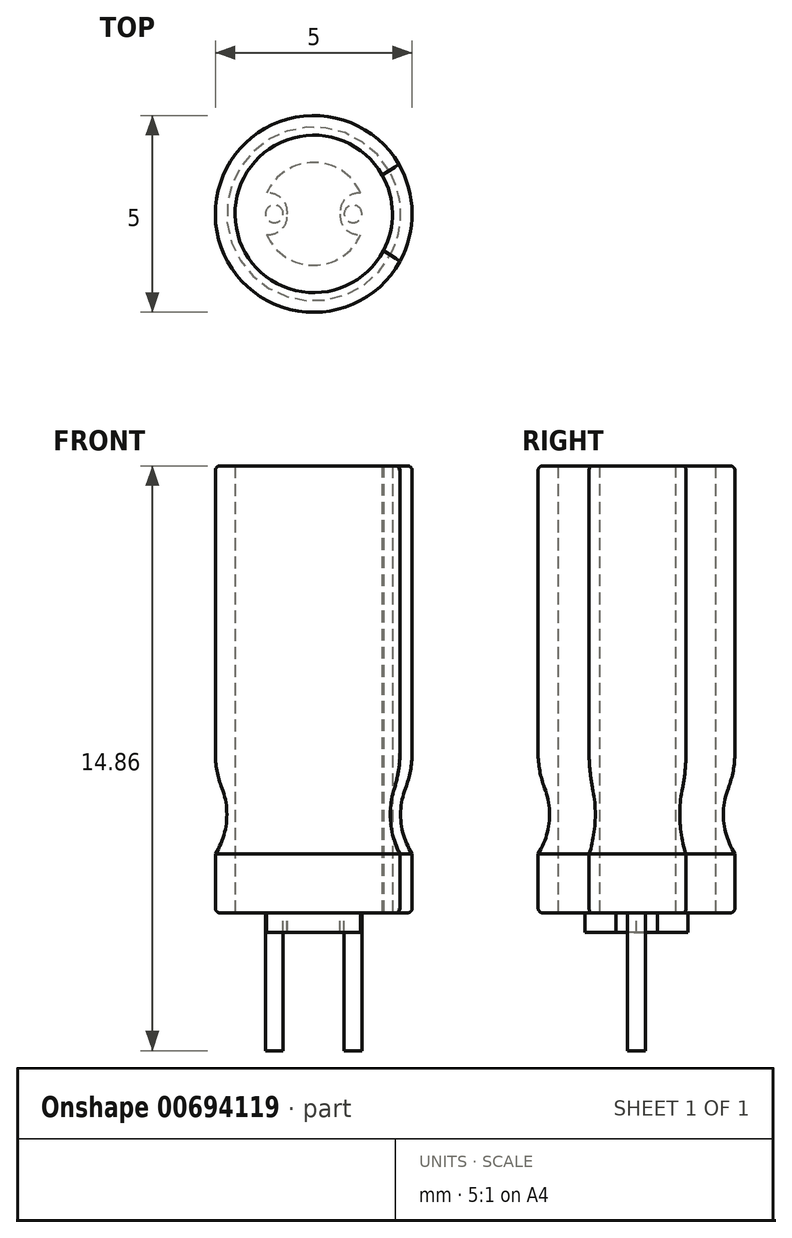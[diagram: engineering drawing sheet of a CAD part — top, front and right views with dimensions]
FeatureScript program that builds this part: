
annotation { "Feature Type Name" : "Feature", "Feature Type Description" : "" }
export const myFeature = defineFeature(function(context is Context, id is Id, definition is map)
    precondition{}
    {
        {
            var Q0;
            Q0=qCreatedBy(makeId("Top.planeOp"),FACE);
            var sketch = newSketch(context, id + "F0", { "sketchPlane" : qUnion([Q0])});
            skCircle(sketch, "E0", {"center": v(0, 0) * mm, "radius": 2.5 * mm});
            skCircle(sketch, "E1", {"center": v(0, 0) * mm, "radius": 2 * mm});
            skLineSegment(sketch, "E2", {"start": v(1.74, 0.99) * mm, "end": v(2.16, 1.26) * mm});
            skLineSegment(sketch, "E3", {"start": v(1.77, -0.93) * mm, "end": v(2.2, -1.2) * mm});
            skSolve(sketch);
        }
        {
            var Q0;
            Q0=qCreatedBy(makeId("Top.planeOp"),FACE);
            var sketch = newSketch(context, id + "F1", { "sketchPlane" : qUnion([Q0])});
            skCircle(sketch, "E4", {"center": v(-1, 0) * mm, "radius": 0.23 * mm});
            skCircle(sketch, "E5", {"center": v(1, 0) * mm, "radius": 0.23 * mm});
            skSolve(sketch);
        }
        {
            var Q0;
            {var subQ0=sQuery(id+"F0.wireOp",EDGE,"E1");var subQ1=makeQuery(id+"F0.imprint","INTERSECT",VERTEX,{"derivedFrom":[subQ0,sQuery(id+"F0.wireOp",EDGE,"E2")]});Q0=makeQuery(id+"F0.imprint","IMPRINT",FACE,{"disambiguationData":[TD([[makeQuery(id+"F0.imprint","IMPRINT",EDGE,{"disambiguationData":[TD([[subQ1,-1.0]])],"derivedFrom":subQ0}),1.0]])]});}
            extrude(context, id + "F2", {"entities" : qUnion([Q0]), "depth" : 11.35 * mm, "offsetDistance" : 25 * mm});
        }
        {
            var Q0;
            {var subQ0=sQuery(id+"F0.wireOp",EDGE,"E2");Q0=makeQuery(id+"F0.imprint","IMPRINT",FACE,{"disambiguationData":[TD([[makeQuery(id+"F0.imprint","IMPRINT",EDGE,{"derivedFrom":subQ0}),1.0]])]});}
            extrude(context, id + "F3", {"entities" : qUnion([Q0]), "depth" : 11.36 * mm, "offsetDistance" : 25 * mm});
        }
        {
            var Q0;
            {var subQ0=sQuery(id+"F0.wireOp",EDGE,"E2");Q0=makeQuery(id+"F0.imprint","IMPRINT",FACE,{"disambiguationData":[TD([[makeQuery(id+"F0.imprint","IMPRINT",EDGE,{"derivedFrom":subQ0}),-1.0]])]});}
            extrude(context, id + "F4", {"entities" : qUnion([Q0]), "depth" : 11.36 * mm, "offsetDistance" : 25 * mm});
        }
        {
            var Q0;
            Q0=makeQuery(id+"F3.opExtrude","CAP_EDGE",EDGE,{"disambiguationData":[OSD([sQuery(id+"F0.wireOp",EDGE,"E0")])],"isStart":false});
            var Q1;
            Q1=makeQuery(id+"F4.opExtrude","CAP_EDGE",EDGE,{"disambiguationData":[OSD([sQuery(id+"F0.wireOp",EDGE,"E0")])],"isStart":false});
            var Q2;
            Q2=makeQuery(id+"F3.opExtrude","CAP_EDGE",EDGE,{"disambiguationData":[OSD([sQuery(id+"F0.wireOp",EDGE,"E0")])],"isStart":true});
            var Q3;
            Q3=makeQuery(id+"F4.opExtrude","CAP_EDGE",EDGE,{"disambiguationData":[OSD([sQuery(id+"F0.wireOp",EDGE,"E0")])],"isStart":true});
            fillet(context, id + "F5", {"entities" : qUnion([Q0, Q1, Q2, Q3]), "radius" : 0.12 * mm, "tangentPropagation" : true, "allowEdgeOverflow" : false});
        }
        {
            var Q0;
            Q0 = qSketchRegion(id + "F1", true);
            extrude(context, id + "F6", {"entities" : qUnion([Q0]), "oppositeDirection" : true, "depth" : 3.5 * mm, "offsetDistance" : 25 * mm});
        }
        {
            var Q0;
            {var subQ0=sQuery(id+"F0.wireOp",EDGE,"E1");var subQ1=makeQuery(id+"F0.imprint","INTERSECT",VERTEX,{"derivedFrom":[subQ0,sQuery(id+"F0.wireOp",EDGE,"E2")]});Q0=makeQuery(id+"F0.imprint","IMPRINT",FACE,{"disambiguationData":[TD([[makeQuery(id+"F0.imprint","IMPRINT",EDGE,{"disambiguationData":[TD([[subQ1,-1.0]])],"derivedFrom":subQ0}),1.0]])]});}
            var sketch = newSketch(context, id + "F7", { "sketchPlane" : qUnion([Q0])});
            skCircle(sketch, "E6", {"center": v(0, 0) * mm, "radius": 1.3 * mm});
            skArc(sketch, "E7", {"start": v(0.67, 0) * mm, "mid": v(0.81, -0.38) * mm, "end": v(1.2, -0.53) * mm});
            skArc(sketch, "E8.MirrorCS", {"start": v(-0.67, 0) * mm, "mid": v(-0.81, -0.38) * mm, "end": v(-1.2, -0.53) * mm});
            skArc(sketch, "E9.MirrorCS", {"start": v(-0.67, 0) * mm, "mid": v(-0.81, 0.38) * mm, "end": v(-1.2, 0.53) * mm});
            skArc(sketch, "E10.MirrorCS", {"start": v(0.67, 0) * mm, "mid": v(0.81, 0.38) * mm, "end": v(1.2, 0.53) * mm});
            skSolve(sketch);
        }
        {
            var Q0;
            {var subQ0=sQuery(id+"F7.wireOp",EDGE,"E7");Q0=makeQuery(id+"F7.imprint","IMPRINT",FACE,{"disambiguationData":[TD([[makeQuery(id+"F7.imprint","IMPRINT",EDGE,{"derivedFrom":subQ0}),-1.0]])]});}
            extrude(context, id + "F8", {"entities" : qUnion([Q0]), "oppositeDirection" : true, "depth" : 0.5 * mm, "offsetDistance" : 25 * mm});
        }
        {
            var Q0;
            Q0=qCreatedBy(makeId("Front.planeOp"),FACE);
            var sketch = newSketch(context, id + "F9", { "sketchPlane" : qUnion([Q0])});
            skLineSegment(sketch, "E11", {"start": v(-2.5, 3.5) * mm, "end": v(-2.5, 1.5) * mm});
            skArc(sketch, "E12", {"start": v(-2.5, 1.5) * mm, "mid": v(-2.2, 2.5) * mm, "end": v(-2.5, 3.5) * mm});
            skSolve(sketch);
        }
        {
            var Q0;
            Q0 = qSketchRegion(id + "F9", true);
            var Q1;
            Q1=makeQuery(id+"F3.opExtrude","SWEPT_FACE",FACE,{"disambiguationData":[OSD([sQuery(id+"F0.wireOp",EDGE,"E0")])]});
            revolve(context, id + "F10", {"operationType" : NewBodyOperationType.REMOVE, "entities" : qUnion([Q0]), "axis" : qUnion([Q1]), "revolveType" : RevolveType.FULL, "oppositeDirection" : true});
        }
        {
            var Q0;
            {var subQ0=sQuery(id+"F9.wireOp",EDGE,"E12");var subQ1=sQuery(id+"F9.wireOp",EDGE,"E11");Q0=makeQuery(id+"F10.boolean.opBoolean","COPY",EDGE,{"disambiguationData":[topologyDisambiguationEdgeConnected([makeQuery(id+"F3.opExtrude","SWEPT_FACE",FACE,{"disambiguationData":[OSD([sQuery(id+"F0.wireOp",EDGE,"E0")])]})])],"derivedFrom":makeQuery(id+"F10.opRevolve","SWEPT_EDGE",EDGE,{"disambiguationData":[OSD([subQ1,subQ0]),TDD([makeQuery(id+"F9.imprint","INTERSECT",VERTEX,{"disambiguationData":[OD(0.0)],"derivedFrom":[subQ1,subQ0]})])]})});}
            var Q1;
            {var subQ0=sQuery(id+"F9.wireOp",EDGE,"E12");var subQ1=sQuery(id+"F9.wireOp",EDGE,"E11");Q1=makeQuery(id+"F10.boolean.opBoolean","COPY",EDGE,{"disambiguationData":[topologyDisambiguationEdgeConnected([makeQuery(id+"F4.opExtrude","SWEPT_FACE",FACE,{"disambiguationData":[OSD([sQuery(id+"F0.wireOp",EDGE,"E0")])]})])],"derivedFrom":makeQuery(id+"F10.opRevolve","SWEPT_EDGE",EDGE,{"disambiguationData":[OSD([subQ1,subQ0]),TDD([makeQuery(id+"F9.imprint","INTERSECT",VERTEX,{"disambiguationData":[OD(0.0)],"derivedFrom":[subQ1,subQ0]})])]})});}
            var Q2;
            {var subQ0=sQuery(id+"F9.wireOp",EDGE,"E12");var subQ1=sQuery(id+"F9.wireOp",EDGE,"E11");Q2=makeQuery(id+"F10.boolean.opBoolean","COPY",EDGE,{"disambiguationData":[topologyDisambiguationEdgeConnected([makeQuery(id+"F3.opExtrude","SWEPT_FACE",FACE,{"disambiguationData":[OSD([sQuery(id+"F0.wireOp",EDGE,"E0")])]})])],"derivedFrom":makeQuery(id+"F10.opRevolve","SWEPT_EDGE",EDGE,{"disambiguationData":[OSD([subQ1,subQ0]),TDD([makeQuery(id+"F9.imprint","INTERSECT",VERTEX,{"disambiguationData":[OD(1.0)],"derivedFrom":[subQ1,subQ0]})])]})});}
            var Q3;
            {var subQ0=sQuery(id+"F9.wireOp",EDGE,"E12");var subQ1=sQuery(id+"F9.wireOp",EDGE,"E11");Q3=makeQuery(id+"F10.boolean.opBoolean","COPY",EDGE,{"disambiguationData":[topologyDisambiguationEdgeConnected([makeQuery(id+"F4.opExtrude","SWEPT_FACE",FACE,{"disambiguationData":[OSD([sQuery(id+"F0.wireOp",EDGE,"E0")])]})])],"derivedFrom":makeQuery(id+"F10.opRevolve","SWEPT_EDGE",EDGE,{"disambiguationData":[OSD([subQ1,subQ0]),TDD([makeQuery(id+"F9.imprint","INTERSECT",VERTEX,{"disambiguationData":[OD(1.0)],"derivedFrom":[subQ1,subQ0]})])]})});}
            fillet(context, id + "F11", {"entities" : qUnion([Q0, Q1, Q2, Q3]), "radius" : 2.5 * mm, "tangentPropagation" : true, "allowEdgeOverflow" : false});
        }
    });
